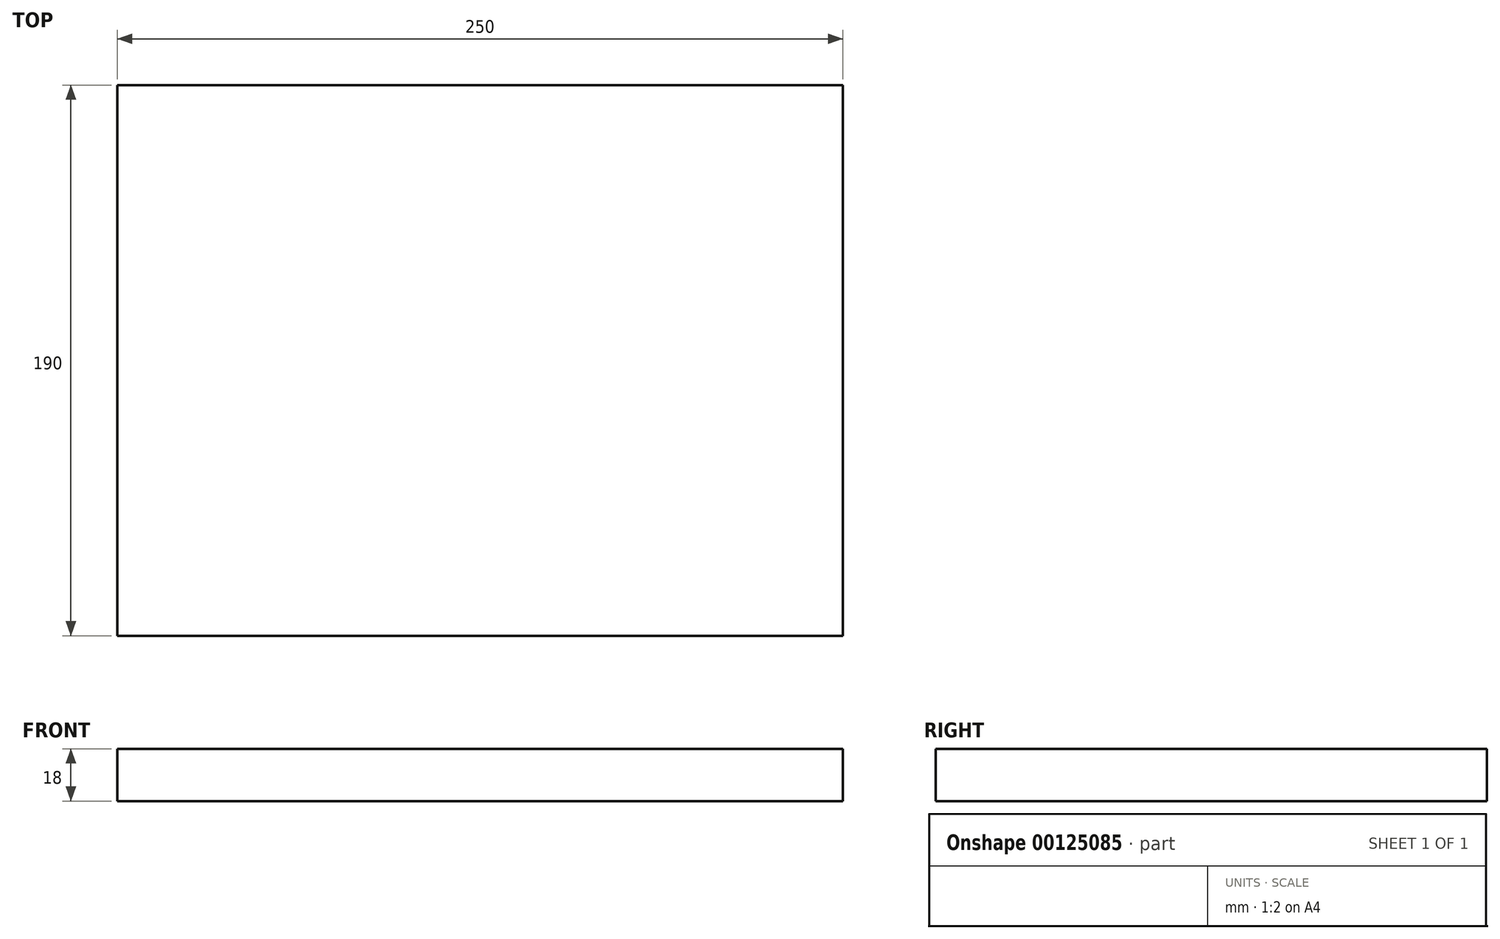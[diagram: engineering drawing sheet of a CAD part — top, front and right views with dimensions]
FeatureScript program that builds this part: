
annotation { "Feature Type Name" : "Feature", "Feature Type Description" : "" }
export const myFeature = defineFeature(function(context is Context, id is Id, definition is map)
    precondition{}
    {
        {
            var Q0;
            Q0=qCreatedBy(makeId("Top.planeOp"),FACE);
            var sketch = newSketch(context, id + "F0", { "sketchPlane" : qUnion([Q0])});
            skLineSegment(sketch, "E0.bottom", {"start": v(125, -95) * mm, "end": v(-125, -95) * mm});
            skLineSegment(sketch, "E0.top", {"start": v(125, 95) * mm, "end": v(-125, 95) * mm});
            skLineSegment(sketch, "E0.left", {"start": v(125, -95) * mm, "end": v(125, 95) * mm});
            skLineSegment(sketch, "E0.right", {"start": v(-125, -95) * mm, "end": v(-125, 95) * mm});
            skPoint(sketch, "E0.middle", {"position": v(0, 0) * mm});
            skSolve(sketch);
        }
        {
            var Q0;
            Q0=makeQuery(id+"F0.imprint","IMPRINT",FACE,{"disambiguationData":[TD([[makeQuery(id+"F0.imprint","IMPRINT",EDGE,{"derivedFrom":sQuery(id+"F0.wireOp",EDGE,"E0.bottom")}),-1.0]])]});
            extrude(context, id + "F1", {"entities" : qUnion([Q0]), "depth" : 18 * mm});
        }
    });
